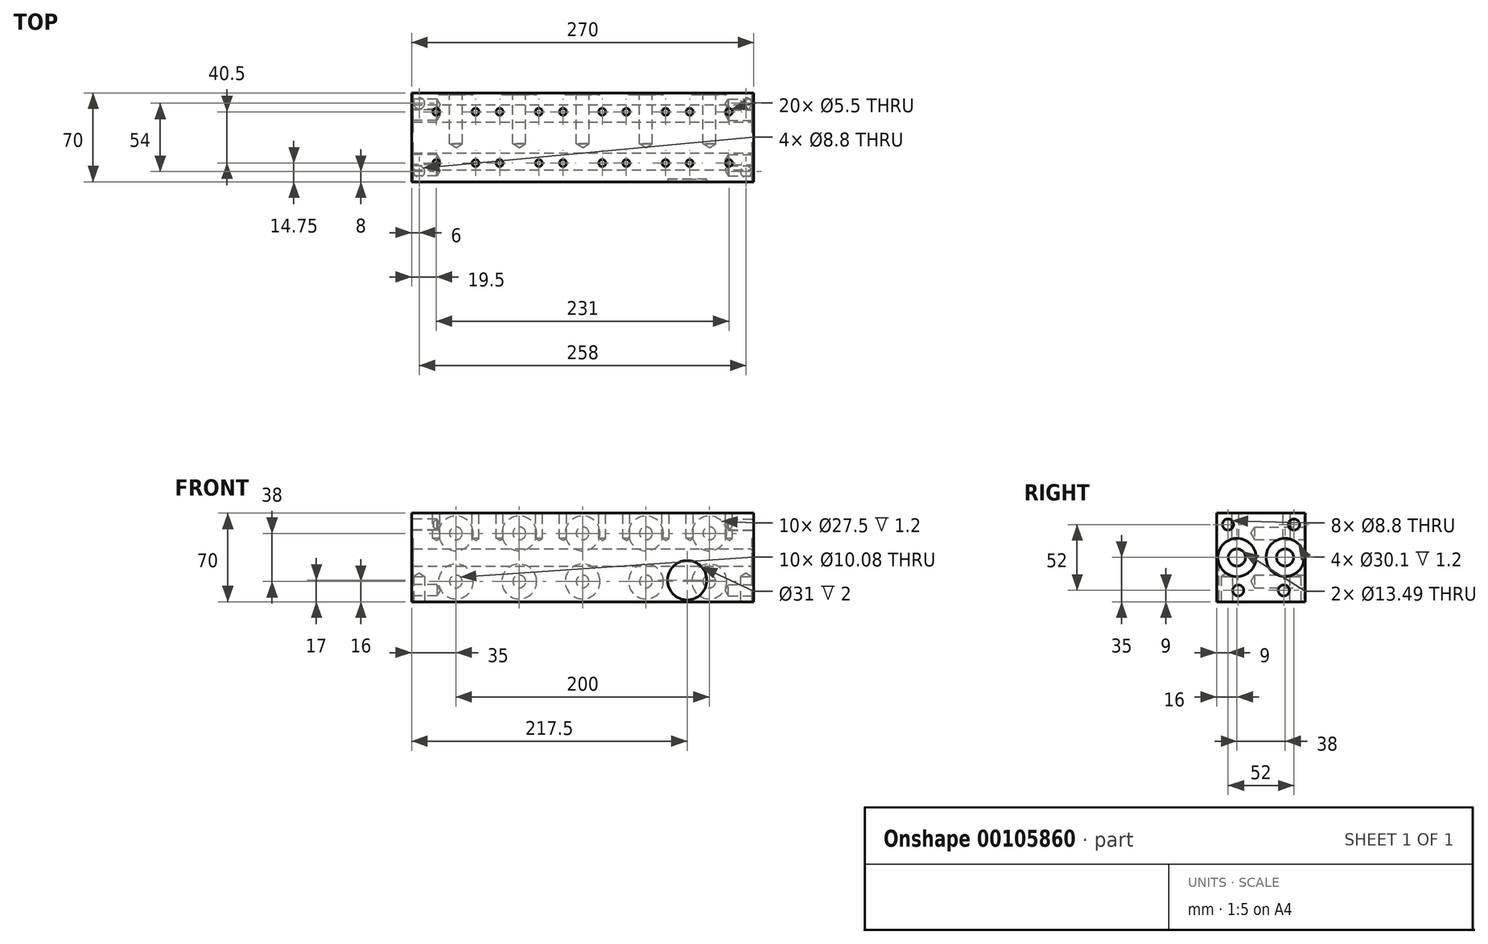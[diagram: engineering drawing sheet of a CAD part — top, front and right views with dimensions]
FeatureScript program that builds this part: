
annotation { "Feature Type Name" : "Feature", "Feature Type Description" : "" }
export const myFeature = defineFeature(function(context is Context, id is Id, definition is map)
    precondition{}
    {
        {
            var Q0;
            Q0=qCreatedBy(makeId("Right.planeOp"),FACE);
            var sketch = newSketch(context, id + "F0", { "sketchPlane" : qUnion([Q0])});
            skLineSegment(sketch, "E0.bottom", {"start": v(-35, -35) * mm, "end": v(35, -35) * mm});
            skLineSegment(sketch, "E0.top", {"start": v(-35, 35) * mm, "end": v(35, 35) * mm});
            skLineSegment(sketch, "E0.left", {"start": v(-35, -35) * mm, "end": v(-35, 35) * mm});
            skLineSegment(sketch, "E0.right", {"start": v(35, -35) * mm, "end": v(35, 35) * mm});
            skPoint(sketch, "E0.middle", {"position": v(0, 0) * mm});
            skSolve(sketch);
        }
        {
            var Q0;
            Q0=makeQuery(id+"F0.imprint","IMPRINT",FACE,{"disambiguationData":[TD([[makeQuery(id+"F0.imprint","IMPRINT",EDGE,{"derivedFrom":sQuery(id+"F0.wireOp",EDGE,"E0.bottom")}),1.0]])]});
            extrude(context, id + "F1", {"entities" : qUnion([Q0]), "depth" : 270 * mm});
        }
        {
            var Q0;
            Q0=makeQuery(id+"F1.opExtrude","CAP_FACE",FACE,{"disambiguationData":[OSD([sQuery(id+"F0.wireOp",EDGE,"E0.bottom"),sQuery(id+"F0.wireOp",EDGE,"E0.top"),sQuery(id+"F0.wireOp",EDGE,"E0.left"),sQuery(id+"F0.wireOp",EDGE,"E0.right")])],"isStart":false});
            var sketch = newSketch(context, id + "F2", { "sketchPlane" : qUnion([Q0])});
            skPoint(sketch, "E1", {"position": v(18, -26) * mm});
            skPoint(sketch, "E2", {"position": v(-18, -26) * mm});
            skPoint(sketch, "E3", {"position": v(-26, 26) * mm});
            skPoint(sketch, "E4", {"position": v(26, 25.94) * mm});
            skCircle(sketch, "E5", {"center": v(-19, 0) * mm, "radius": 15.05 * mm});
            skCircle(sketch, "E6", {"center": v(19, 0) * mm, "radius": 15.05 * mm});
            skSolve(sketch);
        }
        {
            var Q0;
            Q0=sQuery(id+"F2.wireOp",VERTEX,"E5.center");
            var Q1;
            Q1=sQuery(id+"F2.wireOp",VERTEX,"E6.center");
            var Q2;
            Q2=makeQuery(id+"F1.opExtrude","SWEPT_BODY",BODY,{"disambiguationData":[OSD([sQuery(id+"F0.wireOp",EDGE,"E0.bottom"),sQuery(id+"F0.wireOp",EDGE,"E0.top"),sQuery(id+"F0.wireOp",EDGE,"E0.left"),sQuery(id+"F0.wireOp",EDGE,"E0.right")])]});
            hole(context, id + "F3", {"style" : HoleStyle.SIMPLE, "endStyle" : HoleEndStyle.THROUGH, "standardTappedOrClearance" : lookupTablePath({ "standard" : "ANSI", "fit" : "Normal (ASME)", "size" : "1/2", "type" : "Clearance" }), "standardBlindInLast" : lookupTablePath({ "fit" : "Free", "standard" : "ANSI", "size" : "1/2", "type" : "Clearance" }), "holeDiameter" : 13.5 * mm, "locations" : qUnion([Q0, Q1]), "scope" : qUnion([Q2]), "isTappedThrough" : true});
        }
        {
            var Q0;
            Q0=sQuery(id+"F2.wireOp",VERTEX,"E3");
            var Q1;
            Q1=sQuery(id+"F2.wireOp",VERTEX,"E4");
            var Q2;
            Q2=sQuery(id+"F2.wireOp",VERTEX,"E2");
            var Q3;
            Q3=sQuery(id+"F2.wireOp",VERTEX,"E1");
            var Q4;
            Q4=makeQuery(id+"F1.opExtrude","SWEPT_BODY",BODY,{"disambiguationData":[OSD([sQuery(id+"F0.wireOp",EDGE,"E0.bottom"),sQuery(id+"F0.wireOp",EDGE,"E0.top"),sQuery(id+"F0.wireOp",EDGE,"E0.left"),sQuery(id+"F0.wireOp",EDGE,"E0.right")])]});
            hole(context, id + "F4", {"style" : HoleStyle.SIMPLE, "endStyle" : HoleEndStyle.BLIND, "standardTappedOrClearance" : lookupTablePath({ "standard" : "ISO", "fit" : "Normal", "size" : "M8", "type" : "Clearance" }), "standardBlindInLast" : lookupTablePath({ "fit" : "Standard", "standard" : "ISO", "size" : "M8", "type" : "Clearance" }), "holeDiameter" : 8.8 * mm, "holeDepth" : 20 * mm, "locations" : qUnion([Q0, Q1, Q2, Q3]), "scope" : qUnion([Q4])});
        }
        {
            var Q0;
            Q0=qSketchRegion(id+"F2",true);
            extrude(context, id + "F5", {"entities" : qUnion([Q0]), "operationType" : NewBodyOperationType.REMOVE, "oppositeDirection" : true, "depth" : 1.2 * mm});
        }
        {
            var Q0;
            Q0=makeQuery(id+"F1.opExtrude","CAP_FACE",FACE,{"disambiguationData":[OSD([sQuery(id+"F0.wireOp",EDGE,"E0.bottom"),sQuery(id+"F0.wireOp",EDGE,"E0.top"),sQuery(id+"F0.wireOp",EDGE,"E0.left"),sQuery(id+"F0.wireOp",EDGE,"E0.right")])],"isStart":true});
            var sketch = newSketch(context, id + "F6", { "sketchPlane" : qUnion([Q0])});
            skPoint(sketch, "E7", {"position": v(18, -26) * mm});
            skPoint(sketch, "E8", {"position": v(-18, -26) * mm});
            skPoint(sketch, "E9", {"position": v(-26, 25.94) * mm});
            skPoint(sketch, "E10", {"position": v(26, 26) * mm});
            skCircle(sketch, "E11", {"center": v(-19, 0) * mm, "radius": 15.05 * mm});
            skCircle(sketch, "E12", {"center": v(19, 0) * mm, "radius": 15.05 * mm});
            skSolve(sketch);
        }
        {
            var Q0;
            Q0=sQuery(id+"F6.wireOp",VERTEX,"E9");
            var Q1;
            Q1=sQuery(id+"F6.wireOp",VERTEX,"E10");
            var Q2;
            Q2=sQuery(id+"F6.wireOp",VERTEX,"E8");
            var Q3;
            Q3=sQuery(id+"F6.wireOp",VERTEX,"E7");
            var Q4;
            Q4=makeQuery(id+"F1.opExtrude","SWEPT_BODY",BODY,{"disambiguationData":[OSD([sQuery(id+"F0.wireOp",EDGE,"E0.bottom"),sQuery(id+"F0.wireOp",EDGE,"E0.top"),sQuery(id+"F0.wireOp",EDGE,"E0.left"),sQuery(id+"F0.wireOp",EDGE,"E0.right")])]});
            hole(context, id + "F7", {"style" : HoleStyle.SIMPLE, "endStyle" : HoleEndStyle.BLIND, "standardTappedOrClearance" : lookupTablePath({ "standard" : "ISO", "fit" : "Normal", "size" : "M8", "type" : "Clearance" }), "standardBlindInLast" : lookupTablePath({ "fit" : "Standard", "standard" : "ISO", "size" : "M8", "type" : "Clearance" }), "holeDiameter" : 8.8 * mm, "holeDepth" : 20 * mm, "locations" : qUnion([Q0, Q1, Q2, Q3]), "scope" : qUnion([Q4])});
        }
        {
            var Q0;
            Q0=qSketchRegion(id+"F6",true);
            extrude(context, id + "F8", {"entities" : qUnion([Q0]), "operationType" : NewBodyOperationType.REMOVE, "oppositeDirection" : true, "depth" : 1.2 * mm});
        }
        {
            var Q0;
            Q0=makeQuery(id+"F1.opExtrude","SWEPT_FACE",FACE,{"disambiguationData":[OSD([sQuery(id+"F0.wireOp",EDGE,"E0.top")])]});
            var sketch = newSketch(context, id + "F9", { "sketchPlane" : qUnion([Q0])});
            skPoint(sketch, "E13", {"position": v(19.5, 20.25) * mm});
            skPoint(sketch, "E14", {"position": v(19.5, -20.25) * mm});
            skPoint(sketch, "E15", {"position": v(50.5, -20.25) * mm});
            skPoint(sketch, "E16", {"position": v(50.5, 20.25) * mm});
            skPoint(sketch, "E17.1.0.0", {"position": v(69.5, 20.25) * mm});
            skPoint(sketch, "E17.1.0.1", {"position": v(69.5, -20.25) * mm});
            skPoint(sketch, "E17.1.0.2", {"position": v(100.5, -20.25) * mm});
            skPoint(sketch, "E17.1.0.3", {"position": v(100.5, 20.25) * mm});
            skLineSegment(sketch, "E17.direction1", {"start": v(19.5, 20.25) * mm, "end": v(69.5, 20.25) * mm, "construction": true});
            skPoint(sketch, "E18.0.2.0", {"position": v(119.5, 20.25) * mm});
            skPoint(sketch, "E18.1.2.0", {"position": v(119.5, -20.25) * mm});
            skPoint(sketch, "E18.2.2.0", {"position": v(150.5, -20.25) * mm});
            skPoint(sketch, "E18.3.2.0", {"position": v(150.5, 20.25) * mm});
            skPoint(sketch, "E18.0.3.0", {"position": v(169.5, 20.25) * mm});
            skPoint(sketch, "E18.1.3.0", {"position": v(169.5, -20.25) * mm});
            skPoint(sketch, "E18.2.3.0", {"position": v(200.5, -20.25) * mm});
            skPoint(sketch, "E18.3.3.0", {"position": v(200.5, 20.25) * mm});
            skPoint(sketch, "E18.0.4.0", {"position": v(219.5, 20.25) * mm});
            skPoint(sketch, "E18.1.4.0", {"position": v(219.5, -20.25) * mm});
            skPoint(sketch, "E18.2.4.0", {"position": v(250.5, -20.25) * mm});
            skPoint(sketch, "E18.3.4.0", {"position": v(250.5, 20.25) * mm});
            skSolve(sketch);
        }
        {
            var Q0;
            Q0=sQuery(id+"F9.wireOp",VERTEX,"E13");
            var Q1;
            Q1=sQuery(id+"F9.wireOp",VERTEX,"E14");
            var Q2;
            Q2=sQuery(id+"F9.wireOp",VERTEX,"E15");
            var Q3;
            Q3=sQuery(id+"F9.wireOp",VERTEX,"E16");
            var Q4;
            Q4=sQuery(id+"F9.wireOp",VERTEX,"E17.1.0.0");
            var Q5;
            Q5=sQuery(id+"F9.wireOp",VERTEX,"E17.1.0.1");
            var Q6;
            Q6=sQuery(id+"F9.wireOp",VERTEX,"E17.1.0.2");
            var Q7;
            Q7=sQuery(id+"F9.wireOp",VERTEX,"E17.1.0.3");
            var Q8;
            Q8=sQuery(id+"F9.wireOp",VERTEX,"E18.0.2.0");
            var Q9;
            Q9=sQuery(id+"F9.wireOp",VERTEX,"E18.1.2.0");
            var Q10;
            Q10=sQuery(id+"F9.wireOp",VERTEX,"E18.2.2.0");
            var Q11;
            Q11=sQuery(id+"F9.wireOp",VERTEX,"E18.1.3.0");
            var Q12;
            Q12=sQuery(id+"F9.wireOp",VERTEX,"E18.0.3.0");
            var Q13;
            Q13=sQuery(id+"F9.wireOp",VERTEX,"E18.3.2.0");
            var Q14;
            Q14=sQuery(id+"F9.wireOp",VERTEX,"E18.3.3.0");
            var Q15;
            Q15=sQuery(id+"F9.wireOp",VERTEX,"E18.0.4.0");
            var Q16;
            Q16=sQuery(id+"F9.wireOp",VERTEX,"E18.2.3.0");
            var Q17;
            Q17=sQuery(id+"F9.wireOp",VERTEX,"E18.1.4.0");
            var Q18;
            Q18=sQuery(id+"F9.wireOp",VERTEX,"E18.3.4.0");
            var Q19;
            Q19=sQuery(id+"F9.wireOp",VERTEX,"E18.2.4.0");
            var Q20;
            Q20=makeQuery(id+"F1.opExtrude","SWEPT_BODY",BODY,{"disambiguationData":[OSD([sQuery(id+"F0.wireOp",EDGE,"E0.bottom"),sQuery(id+"F0.wireOp",EDGE,"E0.top"),sQuery(id+"F0.wireOp",EDGE,"E0.left"),sQuery(id+"F0.wireOp",EDGE,"E0.right")])]});
            hole(context, id + "F10", {"style" : HoleStyle.SIMPLE, "endStyle" : HoleEndStyle.BLIND, "standardTappedOrClearance" : lookupTablePath({ "standard" : "ISO", "fit" : "Normal", "size" : "M5", "type" : "Clearance" }), "standardBlindInLast" : lookupTablePath({ "fit" : "Standard", "standard" : "ISO", "size" : "M5", "type" : "Clearance" }), "holeDiameter" : 5.5 * mm, "holeDepth" : 20 * mm, "locations" : qUnion([Q0, Q1, Q2, Q3, Q4, Q5, Q6, Q7, Q8, Q9, Q10, Q11, Q12, Q13, Q14, Q15, Q16, Q17, Q18, Q19]), "scope" : qUnion([Q20])});
        }
        {
            var Q0;
            Q0=makeQuery(id+"F1.opExtrude","SWEPT_FACE",FACE,{"disambiguationData":[OSD([sQuery(id+"F0.wireOp",EDGE,"E0.bottom")])]});
            var sketch = newSketch(context, id + "F11", { "sketchPlane" : qUnion([Q0])});
            skPoint(sketch, "E19", {"position": v(6, 27) * mm});
            skPoint(sketch, "E20", {"position": v(6, -27) * mm});
            skPoint(sketch, "E21", {"position": v(264, 27) * mm});
            skPoint(sketch, "E22", {"position": v(264, -27) * mm});
            skSolve(sketch);
        }
        {
            var Q0;
            Q0=sQuery(id+"F11.wireOp",VERTEX,"E19");
            var Q1;
            Q1=sQuery(id+"F11.wireOp",VERTEX,"E20");
            var Q2;
            Q2=sQuery(id+"F11.wireOp",VERTEX,"E21");
            var Q3;
            Q3=sQuery(id+"F11.wireOp",VERTEX,"E22");
            var Q4;
            Q4=makeQuery(id+"F1.opExtrude","SWEPT_BODY",BODY,{"disambiguationData":[OSD([sQuery(id+"F0.wireOp",EDGE,"E0.bottom"),sQuery(id+"F0.wireOp",EDGE,"E0.top"),sQuery(id+"F0.wireOp",EDGE,"E0.left"),sQuery(id+"F0.wireOp",EDGE,"E0.right")])]});
            hole(context, id + "F12", {"style" : HoleStyle.SIMPLE, "endStyle" : HoleEndStyle.BLIND, "standardTappedOrClearance" : lookupTablePath({ "standard" : "ISO", "fit" : "Normal", "size" : "M8", "type" : "Clearance" }), "standardBlindInLast" : lookupTablePath({ "fit" : "Standard", "standard" : "ISO", "size" : "M8", "type" : "Clearance" }), "holeDiameter" : 8.8 * mm, "holeDepth" : 20 * mm, "locations" : qUnion([Q0, Q1, Q2, Q3]), "scope" : qUnion([Q4])});
        }
        {
            var Q0;
            Q0=makeQuery(id+"F1.opExtrude","SWEPT_FACE",FACE,{"disambiguationData":[OSD([sQuery(id+"F0.wireOp",EDGE,"E0.right")])]});
            var sketch = newSketch(context, id + "F13", { "sketchPlane" : qUnion([Q0])});
            skPoint(sketch, "E23", {"position": v(-235, 19) * mm});
            skPoint(sketch, "E24", {"position": v(-235, -19) * mm});
            skPoint(sketch, "E25", {"position": v(-185, 19) * mm});
            skPoint(sketch, "E26", {"position": v(-185, -19) * mm});
            skCircle(sketch, "E27", {"center": v(-235, 19) * mm, "radius": 13.75 * mm});
            skCircle(sketch, "E28.0.1.0", {"center": v(-235, -19) * mm, "radius": 13.75 * mm});
            skCircle(sketch, "E28.1.0.0", {"center": v(-185, 19) * mm, "radius": 13.75 * mm});
            skCircle(sketch, "E28.1.1.0", {"center": v(-185, -19) * mm, "radius": 13.75 * mm});
            skLineSegment(sketch, "E28.direction1", {"start": v(-235, 19) * mm, "end": v(-185, 19) * mm, "construction": true});
            skLineSegment(sketch, "E28.direction2", {"start": v(-235, 19) * mm, "end": v(-235, -19) * mm, "construction": true});
            skCircle(sketch, "E29.0.2.0", {"center": v(-135, 19) * mm, "radius": 13.75 * mm});
            skCircle(sketch, "E29.0.2.1", {"center": v(-135, -19) * mm, "radius": 13.75 * mm});
            skCircle(sketch, "E29.0.3.0", {"center": v(-85, 19) * mm, "radius": 13.75 * mm});
            skCircle(sketch, "E29.0.3.1", {"center": v(-85, -19) * mm, "radius": 13.75 * mm});
            skCircle(sketch, "E29.0.4.0", {"center": v(-35, 19) * mm, "radius": 13.75 * mm});
            skCircle(sketch, "E29.0.4.1", {"center": v(-35, -19) * mm, "radius": 13.75 * mm});
            skSolve(sketch);
        }
        {
            var Q0;
            Q0=sQuery(id+"F13.wireOp",VERTEX,"E23");
            var Q1;
            Q1=sQuery(id+"F13.wireOp",VERTEX,"E25");
            var Q2;
            Q2=sQuery(id+"F13.wireOp",VERTEX,"E26");
            var Q3;
            Q3=sQuery(id+"F13.wireOp",VERTEX,"E24");
            var Q4;
            Q4=sQuery(id+"F13.wireOp",VERTEX,"E29.0.2.1.center");
            var Q5;
            Q5=sQuery(id+"F13.wireOp",VERTEX,"E29.0.2.0.center");
            var Q6;
            Q6=sQuery(id+"F13.wireOp",VERTEX,"E29.0.3.1.center");
            var Q7;
            Q7=sQuery(id+"F13.wireOp",VERTEX,"E29.0.3.0.center");
            var Q8;
            Q8=sQuery(id+"F13.wireOp",VERTEX,"E29.0.4.0.center");
            var Q9;
            Q9=sQuery(id+"F13.wireOp",VERTEX,"E29.0.4.1.center");
            var Q10;
            Q10=makeQuery(id+"F1.opExtrude","SWEPT_BODY",BODY,{"disambiguationData":[OSD([sQuery(id+"F0.wireOp",EDGE,"E0.bottom"),sQuery(id+"F0.wireOp",EDGE,"E0.top"),sQuery(id+"F0.wireOp",EDGE,"E0.left"),sQuery(id+"F0.wireOp",EDGE,"E0.right")])]});
            hole(context, id + "F14", {"style" : HoleStyle.SIMPLE, "endStyle" : HoleEndStyle.BLIND, "standardTappedOrClearance" : lookupTablePath({ "standard" : "ANSI", "fit" : "Normal (ASME)", "size" : "3/8", "type" : "Clearance" }), "standardBlindInLast" : lookupTablePath({ "fit" : "Free", "standard" : "ANSI", "size" : "3/8", "type" : "Clearance" }), "holeDiameter" : 10.08 * mm, "holeDepth" : 40 * mm, "locations" : qUnion([Q0, Q1, Q2, Q3, Q4, Q5, Q6, Q7, Q8, Q9]), "scope" : qUnion([Q10])});
        }
        {
            var Q0;
            Q0=qSketchRegion(id+"F13",true);
            extrude(context, id + "F15", {"entities" : qUnion([Q0]), "operationType" : NewBodyOperationType.REMOVE, "oppositeDirection" : true, "depth" : 1.2 * mm});
        }
        {
            var Q0;
            Q0=makeQuery(id+"F1.opExtrude","SWEPT_FACE",FACE,{"disambiguationData":[OSD([sQuery(id+"F0.wireOp",EDGE,"E0.left")])]});
            var sketch = newSketch(context, id + "F16", { "sketchPlane" : qUnion([Q0])});
            skCircle(sketch, "E30", {"center": v(217.5, -18) * mm, "radius": 15.5 * mm});
            skSolve(sketch);
        }
        {
            var Q0;
            Q0 = qSketchRegion(id + "F16", true);
            extrude(context, id + "F17", {"entities" : qUnion([Q0]), "operationType" : NewBodyOperationType.REMOVE, "oppositeDirection" : true, "depth" : 2 * mm});
        }
    });
